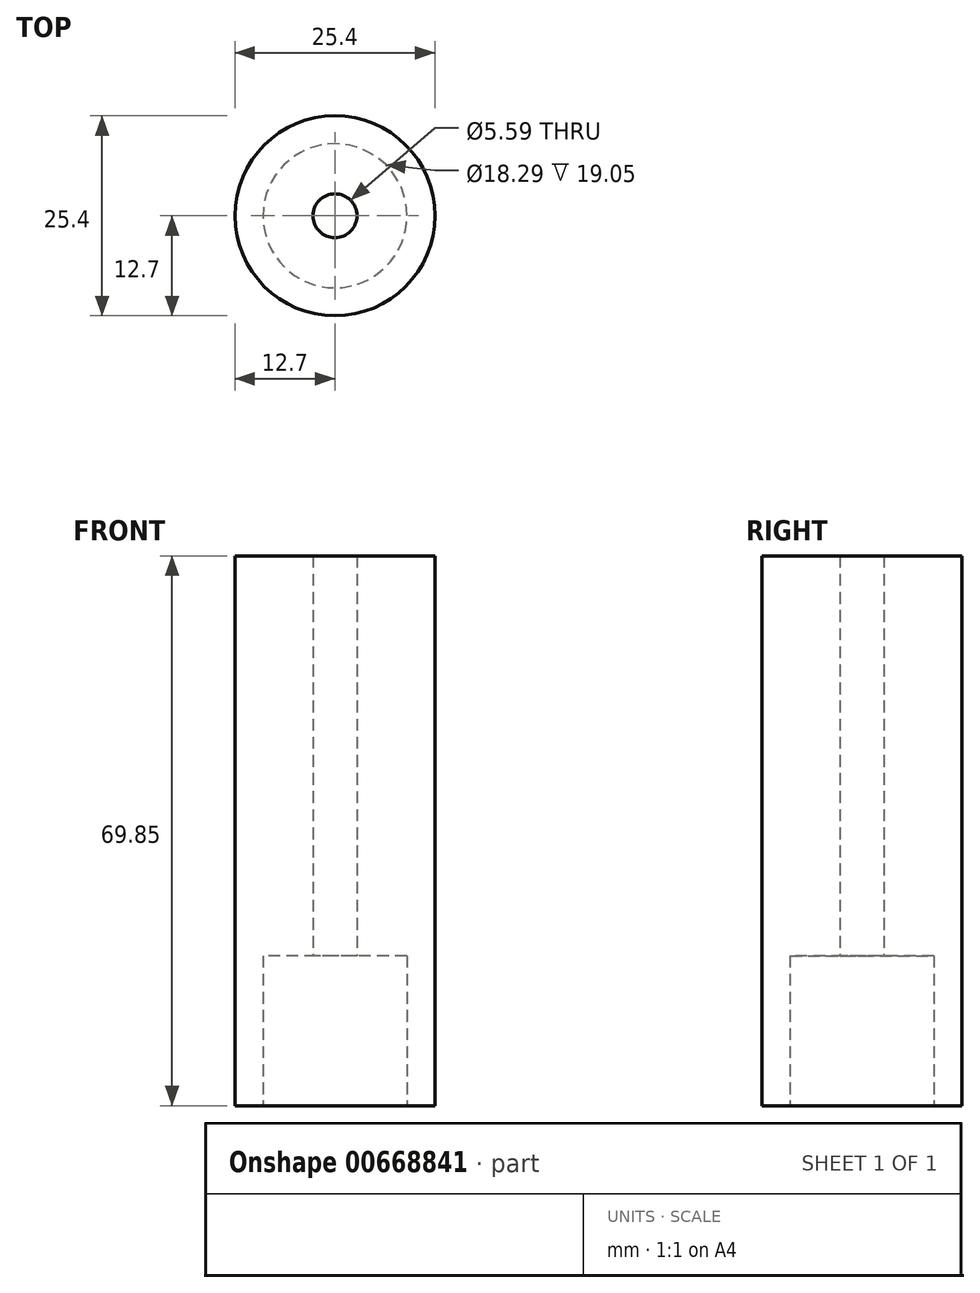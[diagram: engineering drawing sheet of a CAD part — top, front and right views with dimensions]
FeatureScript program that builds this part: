
annotation { "Feature Type Name" : "Feature", "Feature Type Description" : "" }
export const myFeature = defineFeature(function(context is Context, id is Id, definition is map)
    precondition{}
    {
        {
            var Q0;
            Q0=qCreatedBy(makeId("Top.planeOp"),FACE);
            var sketch = newSketch(context, id + "F0", { "sketchPlane" : qUnion([Q0])});
            skCircle(sketch, "E0", {"center": v(0, 0) * mm, "radius": 12.7 * mm});
            skCircle(sketch, "E1", {"center": v(0, 0) * mm, "radius": 9.14 * mm});
            skCircle(sketch, "E2", {"center": v(0, 0) * mm, "radius": 2.8 * mm});
            skSolve(sketch);
        }
        {
            var Q0;
            Q0 = qSketchRegion(id + "F0", true);
            var Q1;
            Q1=makeQuery(id+"F0.imprint","IMPRINT",FACE,{"disambiguationData":[TD([[makeQuery(id+"F0.imprint","IMPRINT",EDGE,{"derivedFrom":sQuery(id+"F0.wireOp",EDGE,"E1")}),1.0]])]});
            var Q2;
            Q2=makeQuery(id+"F0.imprint","IMPRINT",FACE,{"disambiguationData":[TD([[makeQuery(id+"F0.imprint","IMPRINT",EDGE,{"derivedFrom":sQuery(id+"F0.wireOp",EDGE,"E2")}),1.0]])]});
            extrude(context, id + "F1", {"entities" : qUnion([Q0, Q1, Q2]), "depth" : 69.85 * mm, "offsetDistance" : 25.4 * mm});
        }
        {
            var Q0;
            Q0=makeQuery(id+"F0.imprint","IMPRINT",FACE,{"disambiguationData":[TD([[makeQuery(id+"F0.imprint","IMPRINT",EDGE,{"derivedFrom":sQuery(id+"F0.wireOp",EDGE,"E2")}),1.0]])]});
            extrude(context, id + "F2", {"entities" : qUnion([Q0]), "operationType" : NewBodyOperationType.REMOVE, "endBound" : BoundingType.THROUGH_ALL, "depth" : 25.4 * mm, "offsetDistance" : 25.4 * mm});
        }
        {
            var Q0;
            Q0=makeQuery(id+"F0.imprint","IMPRINT",FACE,{"disambiguationData":[TD([[makeQuery(id+"F0.imprint","IMPRINT",EDGE,{"derivedFrom":sQuery(id+"F0.wireOp",EDGE,"E1")}),1.0]])]});
            extrude(context, id + "F3", {"entities" : qUnion([Q0]), "operationType" : NewBodyOperationType.REMOVE, "depth" : 19.05 * mm, "offsetDistance" : 25.4 * mm});
        }
    });
